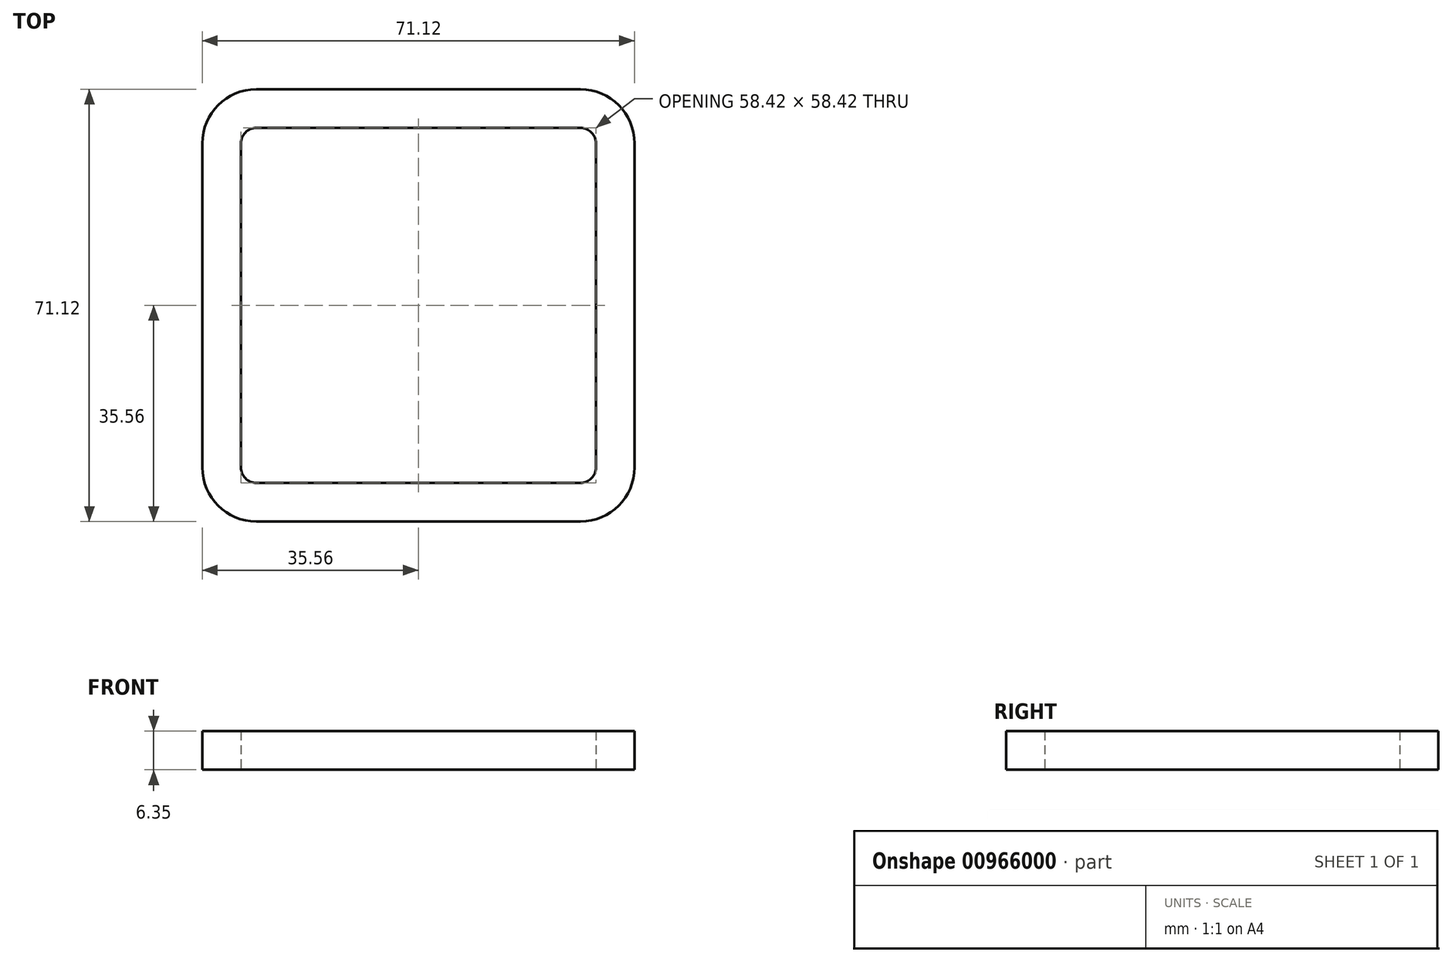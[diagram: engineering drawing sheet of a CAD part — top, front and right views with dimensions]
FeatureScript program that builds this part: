
annotation { "Feature Type Name" : "Feature", "Feature Type Description" : "" }
export const myFeature = defineFeature(function(context is Context, id is Id, definition is map)
    precondition{}
    {
        {
            var Q0;
            Q0=qCreatedBy(makeId("Top.planeOp"),FACE);
            var sketch = newSketch(context, id + "F0", { "sketchPlane" : qUnion([Q0])});
            skLineSegment(sketch, "E0.bottom", {"start": v(-29.21, 29.21) * mm, "end": v(29.21, 29.21) * mm});
            skLineSegment(sketch, "E0.top", {"start": v(-29.21, -29.21) * mm, "end": v(29.21, -29.2) * mm});
            skLineSegment(sketch, "E0.left", {"start": v(-29.21, 29.21) * mm, "end": v(-29.21, -29.21) * mm});
            skLineSegment(sketch, "E0.right", {"start": v(29.2, 29.21) * mm, "end": v(29.21, -29.2) * mm});
            skLineSegment(sketch, "E1.bottom", {"start": v(-35.56, 35.56) * mm, "end": v(35.56, 35.56) * mm});
            skLineSegment(sketch, "E1.top", {"start": v(-35.56, -35.56) * mm, "end": v(35.56, -35.56) * mm});
            skLineSegment(sketch, "E1.left", {"start": v(-35.56, 35.56) * mm, "end": v(-35.56, -35.56) * mm});
            skLineSegment(sketch, "E1.right", {"start": v(35.56, 35.56) * mm, "end": v(35.56, -35.56) * mm});
            skLineSegment(sketch, "E2", {"start": v(-29.21, -29.21) * mm, "end": v(29.21, 29.21) * mm, "construction": true});
            skLineSegment(sketch, "E3", {"start": v(-35.56, 35.56) * mm, "end": v(35.56, -35.56) * mm, "construction": true});
            skSolve(sketch);
        }
        {
            var Q0;
            Q0=makeQuery(id+"F0.imprint","IMPRINT",FACE,{"disambiguationData":[TD([[makeQuery(id+"F0.imprint","IMPRINT",EDGE,{"derivedFrom":sQuery(id+"F0.wireOp",EDGE,"E0.bottom")}),1.0]])]});
            extrude(context, id + "F1", {"entities" : qUnion([Q0]), "depth" : 6.35 * mm, "offsetDistance" : 25.4 * mm});
        }
        {
            var Q0;
            Q0=makeQuery(id+"F1.opExtrude","SWEPT_EDGE",EDGE,{"disambiguationData":[OSD([sQuery(id+"F0.wireOp",EDGE,"E1.top"),sQuery(id+"F0.wireOp",EDGE,"E1.right")])]});
            var Q1;
            Q1=makeQuery(id+"F1.opExtrude","SWEPT_EDGE",EDGE,{"disambiguationData":[OSD([sQuery(id+"F0.wireOp",EDGE,"E1.top"),sQuery(id+"F0.wireOp",EDGE,"E1.left")])]});
            var Q2;
            Q2=makeQuery(id+"F1.opExtrude","SWEPT_EDGE",EDGE,{"disambiguationData":[OSD([sQuery(id+"F0.wireOp",EDGE,"E1.bottom"),sQuery(id+"F0.wireOp",EDGE,"E1.right")])]});
            var Q3;
            Q3=makeQuery(id+"F1.opExtrude","SWEPT_EDGE",EDGE,{"disambiguationData":[OSD([sQuery(id+"F0.wireOp",EDGE,"E1.bottom"),sQuery(id+"F0.wireOp",EDGE,"E1.left")])]});
            fillet(context, id + "F2", {"entities" : qUnion([Q0, Q1, Q2, Q3]), "radius" : 8.9 * mm, "tangentPropagation" : true, "allowEdgeOverflow" : false});
        }
        {
            var Q0;
            Q0=makeQuery(id+"F1.opExtrude","SWEPT_EDGE",EDGE,{"disambiguationData":[OSD([sQuery(id+"F0.wireOp",EDGE,"E0.bottom"),sQuery(id+"F0.wireOp",EDGE,"E0.left")])]});
            var Q1;
            Q1=makeQuery(id+"F1.opExtrude","SWEPT_EDGE",EDGE,{"disambiguationData":[OSD([sQuery(id+"F0.wireOp",EDGE,"E0.top"),sQuery(id+"F0.wireOp",EDGE,"E0.left")])]});
            var Q2;
            Q2=makeQuery(id+"F1.opExtrude","SWEPT_EDGE",EDGE,{"disambiguationData":[OSD([sQuery(id+"F0.wireOp",EDGE,"E0.top"),sQuery(id+"F0.wireOp",EDGE,"E0.right")])]});
            var Q3;
            Q3=makeQuery(id+"F1.opExtrude","SWEPT_EDGE",EDGE,{"disambiguationData":[OSD([sQuery(id+"F0.wireOp",EDGE,"E0.bottom"),sQuery(id+"F0.wireOp",EDGE,"E0.right")])]});
            fillet(context, id + "F3", {"entities" : qUnion([Q0, Q1, Q2, Q3]), "radius" : 2.54 * mm, "tangentPropagation" : true, "allowEdgeOverflow" : false});
        }
    });
